# Revit family: RN 86510 Optiflex-Flowpress-Valvola inclinata
name_source: partatom
category: Rohrzubehör
units: mm (PartAtom-declared; Revit-internal decimal feet)

## family parameters
Arbeitsebenenbasiert = Nein
Beim Laden mit Abzugskörper schneiden = Nein
Bemaßung runder Anschluss = Durchmesser verwenden
Gemeinsam genutzt = Nein
Immer vertikal = Ja
Teiletyp = Ventil - Zerlegung in

## types (7) — shared parameters
1.010.00.2 Blattnummer der Richtlinie = 17
1.010.00.3 Ausgabedatum (Monat) der Richtlinie = 201601
1.010.00.4 Herstellername = R. Nussbaum AG
1.010.00.5 Revisionsdatum der Datei = 20190528
1.010.00.6 Webadresse des Herstellers = http://www.nussbaum.ch
1.100.00.3 Sortiernummer für Anzeigereihenfolge = 1
1.100.00.4 Produktbezeichnung = Absperrarmaturen
1.960/3L.00.8 Link (URL) = https://www.nussbaum.ch
17.700.00.4 Armaturentyp = 1
17.700.00.7 Maximale Betriebstemperatur TB [°C] = 70
17.700.00.8 Maximaler Betriebsdruck (Arbeitsdruck) ps [1.0 · 105 Pa] = 10
Connector Visibility = Nein
EnclosingSpace Visibility = Nein
Hersteller = R. Nussbaum AG
URL = https://www.nussbaum.ch

## per-type parameters (varying)
- DN 12: 1.800.00.3 TGA-Nummer=001056???0000000000000000000020070000000000000000100000000; 1.810.00.3 Hersteller-Bestellnummer=86510.22; 1.810.00.4 DATANORM-Nummer=86510.22; 1.810.00.5 StLB-Nummer=381.151; 1.810.00.6 GTIN-Nummer=7612945734624; 17.700.00.30 Produktbeschreibung=86510.22, Optiflex-Flowpress-Schrägsitzventil, DN=12; 17.700.00.5 Nennweite DN=12; 17.700.00.6 kvs-Wert [m3/h]=3; CONNECTOR0_DIAMETER_dX_0r=15 mm; CONNECTOR0_dX_00=54 mm; CONNECTOR0_dX_01=40 mm; CONNECTOR0_ref_dX=40 mm; CONNECTOR1_DIAMETER_dX_0r=15 mm; CONNECTOR1_dX_00=39 mm; CONNECTOR1_dX_01=53 mm; CONNECTOR1_ref_dX=39 mm; Modell=86510.22; R. Nussbaum AG 86510.22 de Visibility=Ja; R. Nussbaum AG 86510.23 de Visibility=Nein; R. Nussbaum AG 86510.24 de Visibility=Nein; R. Nussbaum AG 86510.25 de Visibility=Nein; R. Nussbaum AG 86510.26 de Visibility=Nein; R. Nussbaum AG 86510.27 de Visibility=Nein; R. Nussbaum AG 86510.28 de Visibility=Nein; Typenkommentare=Optiflex-Flowpress-Schrägsitzventil DN 12
- DN 15: 1.800.00.3 TGA-Nummer=001056???0000000000000000000020070000000000000000200000000; 1.810.00.3 Hersteller-Bestellnummer=86510.23; 1.810.00.4 DATANORM-Nummer=86510.23; 1.810.00.5 StLB-Nummer=381.152; 1.810.00.6 GTIN-Nummer=7612945734631; 17.700.00.30 Produktbeschreibung=86510.23, Optiflex-Flowpress-Schrägsitzventil, DN=15; 17.700.00.5 Nennweite DN=15; 17.700.00.6 kvs-Wert [m3/h]=4.6; CONNECTOR0_DIAMETER_dX_0r=15 mm; CONNECTOR0_dX_00=54 mm; CONNECTOR0_dX_01=40 mm; CONNECTOR0_ref_dX=40 mm; CONNECTOR1_DIAMETER_dX_0r=15 mm; CONNECTOR1_dX_00=40 mm; CONNECTOR1_dX_01=54 mm; CONNECTOR1_ref_dX=40 mm; Modell=86510.23; R. Nussbaum AG 86510.22 de Visibility=Nein; R. Nussbaum AG 86510.23 de Visibility=Ja; R. Nussbaum AG 86510.24 de Visibility=Nein; R. Nussbaum AG 86510.25 de Visibility=Nein; R. Nussbaum AG 86510.26 de Visibility=Nein; R. Nussbaum AG 86510.27 de Visibility=Nein; R. Nussbaum AG 86510.28 de Visibility=Nein; Typenkommentare=Optiflex-Flowpress-Schrägsitzventil DN 15
- DN 20: 1.800.00.3 TGA-Nummer=001056???0000000000000000000020070000000000000000300000000; 1.810.00.3 Hersteller-Bestellnummer=86510.24; 1.810.00.4 DATANORM-Nummer=86510.24; 1.810.00.5 StLB-Nummer=381.153; 1.810.00.6 GTIN-Nummer=7612945734648; 17.700.00.30 Produktbeschreibung=86510.24, Optiflex-Flowpress-Schrägsitzventil, DN=20; 17.700.00.5 Nennweite DN=20; 17.700.00.6 kvs-Wert [m3/h]=11; CONNECTOR0_DIAMETER_dX_0r=20 mm; CONNECTOR0_dX_00=64 mm; CONNECTOR0_dX_01=44 mm; CONNECTOR0_ref_dX=44 mm; CONNECTOR1_DIAMETER_dX_0r=20 mm; CONNECTOR1_dX_00=45 mm; CONNECTOR1_dX_01=65 mm; CONNECTOR1_ref_dX=45 mm; Modell=86510.24; R. Nussbaum AG 86510.22 de Visibility=Nein; R. Nussbaum AG 86510.23 de Visibility=Nein; R. Nussbaum AG 86510.24 de Visibility=Ja; R. Nussbaum AG 86510.25 de Visibility=Nein; R. Nussbaum AG 86510.26 de Visibility=Nein; R. Nussbaum AG 86510.27 de Visibility=Nein; R. Nussbaum AG 86510.28 de Visibility=Nein; Typenkommentare=Optiflex-Flowpress-Schrägsitzventil DN 20
- DN 25: 1.800.00.3 TGA-Nummer=001056???0000000000000000000020070000000000000000400000000; 1.810.00.3 Hersteller-Bestellnummer=86510.25; 1.810.00.4 DATANORM-Nummer=86510.25; 1.810.00.5 StLB-Nummer=381.154; 1.810.00.6 GTIN-Nummer=7612945730688; 17.700.00.30 Produktbeschreibung=86510.25, Optiflex-Flowpress-Schrägsitzventil, DN=25; 17.700.00.5 Nennweite DN=25; 17.700.00.6 kvs-Wert [m3/h]=20.7; CONNECTOR0_DIAMETER_dX_0r=25 mm  [stored 0.082021 ft]; CONNECTOR0_dX_00=78 mm; CONNECTOR0_dX_01=58 mm; CONNECTOR0_ref_dX=58 mm; CONNECTOR1_DIAMETER_dX_0r=25 mm  [stored 0.082021 ft]; CONNECTOR1_dX_00=58 mm; CONNECTOR1_dX_01=78 mm; CONNECTOR1_ref_dX=58 mm; Modell=86510.25; R. Nussbaum AG 86510.22 de Visibility=Nein; R. Nussbaum AG 86510.23 de Visibility=Nein; R. Nussbaum AG 86510.24 de Visibility=Nein; R. Nussbaum AG 86510.25 de Visibility=Ja; R. Nussbaum AG 86510.26 de Visibility=Nein; R. Nussbaum AG 86510.27 de Visibility=Nein; R. Nussbaum AG 86510.28 de Visibility=Nein; Typenkommentare=Optiflex-Flowpress-Schrägsitzventil DN 25
- DN 32: 1.800.00.3 TGA-Nummer=001056???0000000000000000000020070000000000000000500000000; 1.810.00.3 Hersteller-Bestellnummer=86510.26; 1.810.00.4 DATANORM-Nummer=86510.26; 1.810.00.5 StLB-Nummer=381.155; 1.810.00.6 GTIN-Nummer=7612945734808; 17.700.00.30 Produktbeschreibung=86510.26, Optiflex-Flowpress-Schrägsitzventil, DN=32; 17.700.00.5 Nennweite DN=32; 17.700.00.6 kvs-Wert [m3/h]=35.5; CONNECTOR0_DIAMETER_dX_0r=32 mm; CONNECTOR0_dX_00=91 mm; CONNECTOR0_dX_01=65 mm; CONNECTOR0_ref_dX=65 mm; CONNECTOR1_DIAMETER_dX_0r=32 mm; CONNECTOR1_dX_00=65 mm; CONNECTOR1_dX_01=91 mm; CONNECTOR1_ref_dX=65 mm; Modell=86510.26; R. Nussbaum AG 86510.22 de Visibility=Nein; R. Nussbaum AG 86510.23 de Visibility=Nein; R. Nussbaum AG 86510.24 de Visibility=Nein; R. Nussbaum AG 86510.25 de Visibility=Nein; R. Nussbaum AG 86510.26 de Visibility=Ja; R. Nussbaum AG 86510.27 de Visibility=Nein; R. Nussbaum AG 86510.28 de Visibility=Nein; Typenkommentare=Optiflex-Flowpress-Schrägsitzventil DN 32
- DN 40: 1.800.00.3 TGA-Nummer=001056???0000000000000000000020070000000000000000600000000; 1.810.00.3 Hersteller-Bestellnummer=86510.27; 1.810.00.4 DATANORM-Nummer=86510.27; 1.810.00.6 GTIN-Nummer=7612945747211; 17.700.00.30 Produktbeschreibung=86510.27, Optiflex-Flowpress-Schrägsitzventil, DN=40; 17.700.00.5 Nennweite DN=40; 17.700.00.6 kvs-Wert [m3/h]=59.6; CONNECTOR0_DIAMETER_dX_0r=40 mm; CONNECTOR0_dX_00=99 mm; CONNECTOR0_dX_01=73 mm; CONNECTOR0_ref_dX=73 mm; CONNECTOR1_DIAMETER_dX_0r=40 mm; CONNECTOR1_dX_00=73 mm; CONNECTOR1_dX_01=99 mm; CONNECTOR1_ref_dX=73 mm; Modell=86510.27; R. Nussbaum AG 86510.22 de Visibility=Nein; R. Nussbaum AG 86510.23 de Visibility=Nein; R. Nussbaum AG 86510.24 de Visibility=Nein; R. Nussbaum AG 86510.25 de Visibility=Nein; R. Nussbaum AG 86510.26 de Visibility=Nein; R. Nussbaum AG 86510.27 de Visibility=Ja; R. Nussbaum AG 86510.28 de Visibility=Nein; Typenkommentare=Optiflex-Flowpress-Schrägsitzventil DN 40
- DN 50: 1.800.00.3 TGA-Nummer=001056???0000000000000000000020070000000000000000700000000; 1.810.00.3 Hersteller-Bestellnummer=86510.28; 1.810.00.4 DATANORM-Nummer=86510.28; 1.810.00.6 GTIN-Nummer=7612945747228; 17.700.00.30 Produktbeschreibung=86510.28, Optiflex-Flowpress-Schrägsitzventil, DN=50; 17.700.00.5 Nennweite DN=50; 17.700.00.6 kvs-Wert [m3/h]=98.5; CONNECTOR0_DIAMETER_dX_0r=50 mm; CONNECTOR0_dX_00=114 mm; CONNECTOR0_dX_01=86 mm; CONNECTOR0_ref_dX=86 mm; CONNECTOR1_DIAMETER_dX_0r=50 mm; CONNECTOR1_dX_00=86 mm; CONNECTOR1_dX_01=114 mm; CONNECTOR1_ref_dX=86 mm; Modell=86510.28; R. Nussbaum AG 86510.22 de Visibility=Nein; R. Nussbaum AG 86510.23 de Visibility=Nein; R. Nussbaum AG 86510.24 de Visibility=Nein; R. Nussbaum AG 86510.25 de Visibility=Nein; R. Nussbaum AG 86510.26 de Visibility=Nein; R. Nussbaum AG 86510.27 de Visibility=Nein; R. Nussbaum AG 86510.28 de Visibility=Ja; Typenkommentare=Optiflex-Flowpress-Schrägsitzventil DN 50

note: [stored X ft] marks values corroborated as IEEE doubles in the binary element streams (Revit-internal decimal feet)

## geometry (parser evidence)
native form markers: Sweep x1
no freeform markers — native parametric forms only
